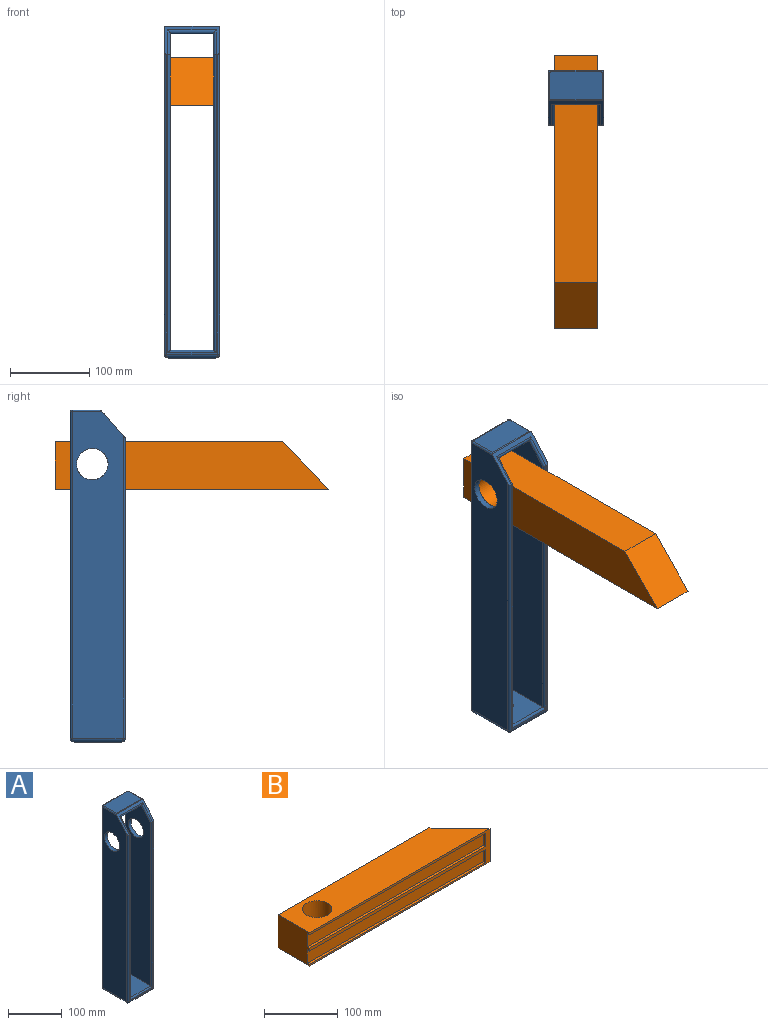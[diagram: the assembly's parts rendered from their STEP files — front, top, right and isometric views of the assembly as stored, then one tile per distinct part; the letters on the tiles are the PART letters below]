
ASSEMBLY  parts=2 mates=1
PART A: 44 faces, bbox 70x70x420 mm
  f0: cylinder r=5mm len=10mm, axis (0,0,-1), area 157.1mm2, adj f17,f19
  f1: plane 413x64mm, normal (0,1,0), area 2596mm2, adj f10,f20,f22,f28,f29,f30,f31,f42
  f2: cylinder r=20mm len=40mm, axis (1,0,0), area 942.5mm2, adj f5,f16
  f3: plane 66x35.66mm, normal (0,0,1), area 2353.2mm2, adj f38,f39,f40,f41,f42,f43
  f4: plane 379.08x64mm, normal (0,-1,0), area 1259.2mm2, adj f9,f13,f24,f26,f35,f36,f37
  f5: plane 413x64mm, normal (1,0,0), area 24768.6mm2, adj f2,f9,f12,f20,f24,f41
  f6: plane 413x64mm, normal (-1,0,0), area 24768.6mm2, adj f8,f9,f11,f22,f26,f38
  f7: plane 60x60mm, normal (0,0,-1), area 3423.3mm2, adj f10,f11,f12,f13,f18
  f8: cylinder r=20mm len=40mm, axis (1,0,0), area 942.5mm2, adj f6,f14
  f9: plane 70x35.24mm, normal (0,-0.75,0.66), area 766.9mm2, adj f4,f5,f6,f24,f26,f32,f33,f34
  f10: cylinder r=5mm len=64mm, axis (1,0,0), area 491.2mm2, adj f1,f7,f21,f23
  f11: cylinder r=5mm len=64mm, axis (0,1,0), area 491.2mm2, adj f6,f7,f23,f27
  f12: cylinder r=5mm len=64mm, axis (0,-1,0), area 491.2mm2, adj f5,f7,f21,f25
  f13: cylinder r=5mm len=64mm, axis (-1,0,0), area 491.2mm2, adj f4,f7,f25,f27
  f14: plane 400.74x65mm, normal (1,0,0), area 24424mm2, adj f8,f15,f17,f29,f32,f34,f36
  f15: plane 55x38.71mm, normal (0,0,-1), area 2128.9mm2, adj f14,f16,f31,f32
  f16: plane 400.74x65mm, normal (-1,0,0), area 24424mm2, adj f2,f15,f17,f30,f32,f33,f35
  f17: plane 65x55mm, normal (0,0,1), area 3496.5mm2, adj f0,f14,f16,f28,f37
  f18: cylinder r=7.5mm len=15mm, axis (0,0,-1), area 235.6mm2, adj f7,f19
  f19: plane 15x15mm, normal (0,0,-1), area 98.2mm2, adj f0,f18
  f20: cylinder r=3mm len=413mm, axis (0,0,1), area 1946.2mm2, adj f1,f5,f21,f43
  f21: bspline ~5.26x5mm, area 24.5mm2, adj f10,f12,f20
  f22: cylinder r=3mm len=413mm, axis (0,0,-1), area 1946.2mm2, adj f1,f6,f23,f40
  f23: bspline ~6.03x5mm, area 24.5mm2, adj f10,f11,f22
  f24: cylinder r=3mm len=382.51mm, axis (0,0,-1), area 1792.3mm2, adj f4,f5,f9,f25
  f25: bspline ~5.26x5mm, area 24.5mm2, adj f12,f13,f24
  f26: cylinder r=3mm len=382.51mm, axis (0,0,1), area 1792.3mm2, adj f4,f6,f9,f27
  f27: bspline ~6.03x5mm, area 24.5mm2, adj f11,f13,f26
  f28: cylinder r=2mm len=59mm, axis (-1,0,0), area 177.4mm2, adj f1,f17,f29,f30
  f29: cylinder r=2mm len=404mm, axis (0,0,1), area 1261.2mm2, adj f1,f14,f28,f31
  f30: cylinder r=2mm len=404mm, axis (0,0,-1), area 1261.2mm2, adj f1,f16,f28,f31
  f31: cylinder r=2mm len=59mm, axis (1,0,0), area 177.4mm2, adj f1,f15,f29,f30
  f32: cylinder r=3mm len=61mm, axis (1,0,0), area 388.1mm2, adj f9,f14,f15,f16,f33,f34
  f33: cylinder r=3mm len=32.87mm, axis (0,-0.66,-0.75), area 182.5mm2, adj f9,f16,f32,f35
  f34: cylinder r=3mm len=32.87mm, axis (0,0.66,0.75), area 182.5mm2, adj f9,f14,f32,f36
  f35: cylinder r=3mm len=377.08mm, axis (0,0,-1), area 1766mm2, adj f4,f16,f33,f37
  f36: cylinder r=3mm len=377.08mm, axis (0,0,1), area 1766mm2, adj f4,f14,f34,f37
  f37: cylinder r=3mm len=61mm, axis (-1,0,0), area 269.5mm2, adj f4,f17,f35,f36
  f38: cylinder r=2mm len=37.32mm, axis (0,-1,0), area 113.2mm2, adj f3,f6,f9,f39,f40
  f39: cylinder r=2mm len=69.01mm, axis (-1,0,0), area 115.2mm2, adj f3,f9,f38,f41
  f40: torus R=1mm, axis (0,0,1), area 11.2mm2, adj f3,f22,f38,f42
  f41: cylinder r=2mm len=37.32mm, axis (0,1,0), area 113.2mm2, adj f3,f5,f9,f39,f43
  f42: cylinder r=2mm len=64mm, axis (-1,0,0), area 201.1mm2, adj f1,f3,f40,f43
  f43: torus R=1mm, axis (0,0,1), area 11.2mm2, adj f3,f20,f41,f42
PART B: 15 faces, bbox 346.1x60x55 mm
  f0: plane 346.09x60mm, normal (0,0,-1), area 17763.7mm2, adj f1,f3,f4,f13,f14
  f1: plane 346.09x55mm, normal (0,-1,0), area 4191.2mm2, adj f0,f2,f4,f5,f6,f7,f9,f10
  f2: plane 346.09x60mm, normal (0,0,1), area 17763.7mm2, adj f1,f3,f4,f13,f14
  f3: plane 287.92x55mm, normal (0,1,0), area 15835.8mm2, adj f0,f2,f4,f14
  f4: plane 60x58.16mm, normal (0.72,0.7,0), area 4596.1mm2, adj f0,f1,f2,f3
  f5: plane 337.39x4mm, normal (0,0,-1), area 1349.6mm2, adj f1,f7,f8,f14
  f6: plane 337.39x4mm, normal (0,0,1), area 1349.6mm2, adj f1,f7,f8,f14
  f7: plane 22x4mm, normal (-1,0,0), area 88mm2, adj f1,f5,f6,f8
  f8: plane 337.39x22mm, normal (0,-1,0), area 7422.6mm2, adj f5,f6,f7,f14
  f9: plane 337.32x4mm, normal (0,0,1), area 1349.3mm2, adj f1,f10,f12,f14
  f10: plane 22x4mm, normal (-1,0,0), area 88mm2, adj f1,f9,f11,f12
  f11: plane 337.32x4mm, normal (0,0,-1), area 1349.3mm2, adj f1,f10,f12,f14
  f12: plane 337.32x22mm, normal (0,-1,0), area 7421.1mm2, adj f9,f10,f11,f14
  f13: cylinder r=20mm len=55mm, axis (0,0,-1), area 6911.5mm2, adj f0,f2
  f14: plane 60x55mm, normal (-1,0,0), area 3124mm2, adj f0,f1,f2,f3,f5,f6,f8,f9
PLACE A t=(-94.76,88.08,11.89)mm
PLACE B rot(axis=(0.58,-0.58,-0.58),120deg) t=(-69.98,-3.02,433.19)mm
MATE revolute B.f13 <-> A.f2  axis (-1,0,0) through (-124.98,98.6,363.35)mm
